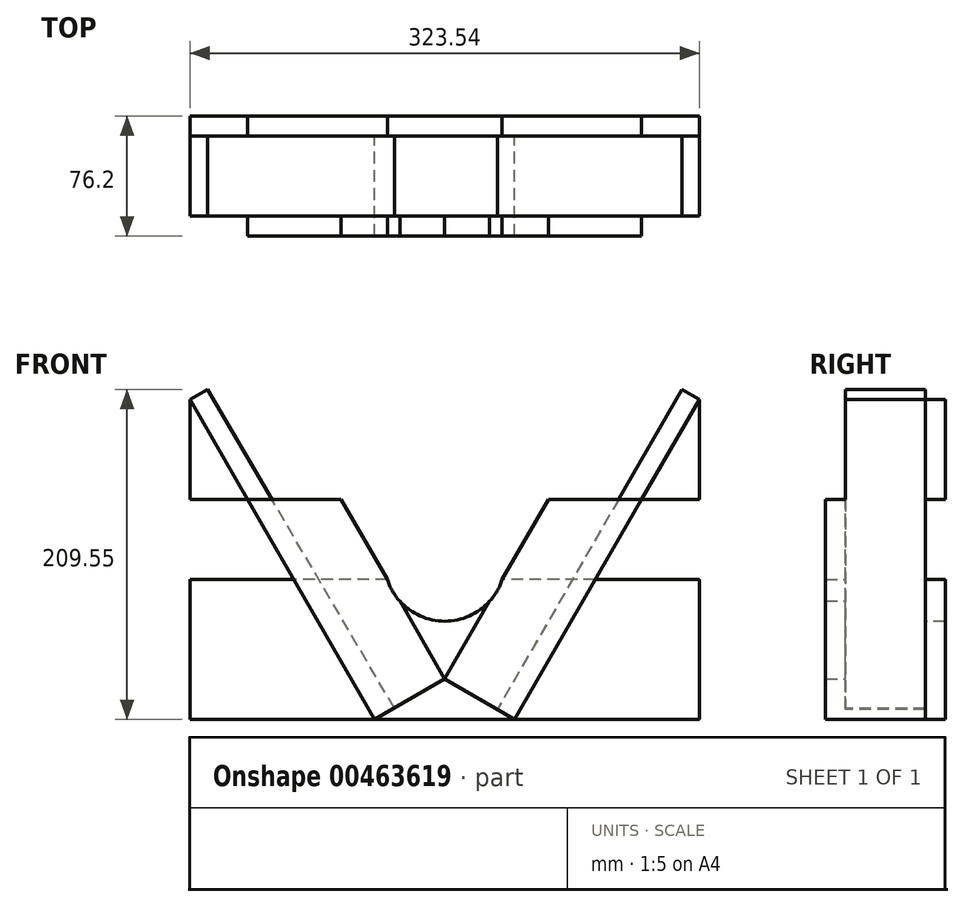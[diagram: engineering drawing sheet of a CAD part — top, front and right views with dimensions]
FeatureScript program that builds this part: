
annotation { "Feature Type Name" : "Feature", "Feature Type Description" : "" }
export const myFeature = defineFeature(function(context is Context, id is Id, definition is map)
    precondition{}
    {
        {
            var Q0;
            Q0=qCreatedBy(makeId("Front.planeOp"),FACE);
            var sketch = newSketch(context, id + "F0", { "sketchPlane" : qUnion([Q0])});
            skLineSegment(sketch, "E0.bottom", {"start": v(44.45, 101.6) * mm, "end": v(-44.45, 101.6) * mm});
            skLineSegment(sketch, "E0.top", {"start": v(44.45, -101.6) * mm, "end": v(-44.45, -101.6) * mm});
            skLineSegment(sketch, "E0.left", {"start": v(44.45, 101.6) * mm, "end": v(44.45, -101.6) * mm});
            skLineSegment(sketch, "E0.right", {"start": v(-44.45, 101.6) * mm, "end": v(-44.45, -101.6) * mm});
            skPoint(sketch, "E0.middle", {"position": v(0, 0) * mm});
            skLineSegment(sketch, "E1", {"start": v(-44.45, -101.6) * mm, "end": v(-161.77, 101.6) * mm});
            skLineSegment(sketch, "E2", {"start": v(44.45, -101.6) * mm, "end": v(161.77, 101.6) * mm});
            skLineSegment(sketch, "E3", {"start": v(-44.45, 101.6) * mm, "end": v(-161.77, 101.6) * mm});
            skLineSegment(sketch, "E4", {"start": v(44.45, 101.6) * mm, "end": v(161.77, 101.6) * mm});
            skLineSegment(sketch, "E5", {"start": v(44.45, -101.6) * mm, "end": v(0, -75.94) * mm});
            skLineSegment(sketch, "E6", {"start": v(0, -75.94) * mm, "end": v(117.42, 127.44) * mm});
            skLineSegment(sketch, "E7", {"start": v(117.42, 127.44) * mm, "end": v(161.77, 101.6) * mm});
            skLineSegment(sketch, "E8", {"start": v(-44.45, -101.6) * mm, "end": v(0, -75.94) * mm});
            skLineSegment(sketch, "E9", {"start": v(0, -75.94) * mm, "end": v(-117.34, 127.3) * mm});
            skLineSegment(sketch, "E10", {"start": v(-117.34, 127.3) * mm, "end": v(-161.77, 101.6) * mm});
            skLineSegment(sketch, "E11.bottom", {"start": v(161.77, 101.6) * mm, "end": v(-161.77, 101.6) * mm});
            skLineSegment(sketch, "E11.top", {"start": v(161.77, 38.1) * mm, "end": v(-161.77, 38.1) * mm});
            skLineSegment(sketch, "E11.left", {"start": v(161.77, 101.6) * mm, "end": v(161.77, 38.1) * mm});
            skLineSegment(sketch, "E11.right", {"start": v(-161.77, 101.6) * mm, "end": v(-161.77, 38.1) * mm});
            skLineSegment(sketch, "E12", {"start": v(102.5, 101.6) * mm, "end": v(161.77, 101.6) * mm});
            skLineSegment(sketch, "E13", {"start": v(-103.1, 101.6) * mm, "end": v(-161.77, 101.6) * mm});
            skLineSegment(sketch, "E14", {"start": v(-161.77, 101.6) * mm, "end": v(-103.1, 101.6) * mm});
            skLineSegment(sketch, "E15.bottom", {"start": v(161.77, -101.6) * mm, "end": v(-161.77, -101.6) * mm});
            skLineSegment(sketch, "E15.top", {"start": v(161.77, -12.7) * mm, "end": v(-161.77, -12.7) * mm});
            skLineSegment(sketch, "E15.left", {"start": v(161.77, -101.6) * mm, "end": v(161.77, -12.7) * mm});
            skLineSegment(sketch, "E15.right", {"start": v(-161.77, -101.6) * mm, "end": v(-161.77, -12.7) * mm});
            skLineSegment(sketch, "E16", {"start": v(44.45, 101.6) * mm, "end": v(44.45, 38.1) * mm});
            skLineSegment(sketch, "E17", {"start": v(-44.45, 101.6) * mm, "end": v(-44.45, 38.1) * mm});
            skArc(sketch, "E18", {"start": v(-36.5, -12.7) * mm, "mid": v(0, -39.2) * mm, "end": v(36.5, -12.7) * mm});
            skPoint(sketch, "E18.startSnap0", {"position": v(0, -12.7) * mm});
            skPoint(sketch, "E18.endSnap0", {"position": v(0, -12.7) * mm});
            skSolve(sketch);
        }
        {
            var Q0;
            {var subQ0=sQuery(id+"F0.wireOp",EDGE,"E2");Q0=makeQuery(id+"F0.imprint","IMPRINT",FACE,{"disambiguationData":[TD([[makeQuery(id+"F0.imprint","IMPRINT",EDGE,{"derivedFrom":subQ0}),1.0]])]});}
            var Q1;
            {var subQ0=sQuery(id+"F0.wireOp",EDGE,"E5");Q1=makeQuery(id+"F0.imprint","IMPRINT",FACE,{"disambiguationData":[TD([[makeQuery(id+"F0.imprint","IMPRINT",EDGE,{"derivedFrom":subQ0}),-1.0]])]});}
            var Q2;
            {var subQ0=sQuery(id+"F0.wireOp",EDGE,"E1");Q2=makeQuery(id+"F0.imprint","IMPRINT",FACE,{"disambiguationData":[TD([[makeQuery(id+"F0.imprint","IMPRINT",EDGE,{"derivedFrom":subQ0}),-1.0]])]});}
            var Q3;
            {var subQ0=sQuery(id+"F0.wireOp",EDGE,"E8");Q3=makeQuery(id+"F0.imprint","IMPRINT",FACE,{"disambiguationData":[TD([[makeQuery(id+"F0.imprint","IMPRINT",EDGE,{"derivedFrom":subQ0}),1.0]])]});}
            var Q4;
            {var subQ5=sQuery(id+"F0.wireOp",EDGE,"E14");Q4=makeQuery(id+"F0.imprint","IMPRINT",FACE,{"disambiguationData":[TD([[makeQuery(id+"F0.imprint","IMPRINT",EDGE,{"derivedFrom":subQ5}),-1.0]])]});}
            var Q5;
            {var subQ3=sQuery(id+"F0.wireOp",EDGE,"E9");var subQ5=sQuery(id+"F0.wireOp",EDGE,"E0.right");var subQ6=makeQuery(id+"F0.imprint","INTERSECT",VERTEX,{"derivedFrom":[subQ5,subQ3]});Q5=makeQuery(id+"F0.imprint","IMPRINT",FACE,{"disambiguationData":[TD([[makeQuery(id+"F0.imprint","IMPRINT",EDGE,{"disambiguationData":[TD([[subQ6,-1.0]])],"derivedFrom":subQ5}),-1.0]])]});}
            var Q6;
            {var subQ3=sQuery(id+"F0.wireOp",EDGE,"E6");var subQ5=sQuery(id+"F0.wireOp",EDGE,"E0.left");var subQ6=makeQuery(id+"F0.imprint","INTERSECT",VERTEX,{"derivedFrom":[subQ5,subQ3]});Q6=makeQuery(id+"F0.imprint","IMPRINT",FACE,{"disambiguationData":[TD([[makeQuery(id+"F0.imprint","IMPRINT",EDGE,{"disambiguationData":[TD([[subQ6,-1.0]])],"derivedFrom":subQ5}),1.0]])]});}
            var Q7;
            {var subQ0=sQuery(id+"F0.wireOp",EDGE,"E6");var subQ1=sQuery(id+"F0.wireOp",EDGE,"E0.left");var subQ2=makeQuery(id+"F0.imprint","INTERSECT",VERTEX,{"derivedFrom":[subQ1,subQ0]});Q7=makeQuery(id+"F0.imprint","IMPRINT",FACE,{"disambiguationData":[TD([[makeQuery(id+"F0.imprint","IMPRINT",EDGE,{"disambiguationData":[TD([[subQ2,-1.0]])],"derivedFrom":subQ1}),-1.0]])]});}
            var Q8;
            {var subQ0=sQuery(id+"F0.wireOp",EDGE,"E9");var subQ1=sQuery(id+"F0.wireOp",EDGE,"E0.right");var subQ2=makeQuery(id+"F0.imprint","INTERSECT",VERTEX,{"derivedFrom":[subQ1,subQ0]});Q8=makeQuery(id+"F0.imprint","IMPRINT",FACE,{"disambiguationData":[TD([[makeQuery(id+"F0.imprint","IMPRINT",EDGE,{"disambiguationData":[TD([[subQ2,-1.0]])],"derivedFrom":subQ1}),1.0]])]});}
            var Q9;
            {var subQ0=sQuery(id+"F0.wireOp",EDGE,"E12");Q9=makeQuery(id+"F0.imprint","IMPRINT",FACE,{"disambiguationData":[TD([[makeQuery(id+"F0.imprint","IMPRINT",EDGE,{"derivedFrom":subQ0}),-1.0]])]});}
            extrude(context, id + "F1", {"entities" : qUnion([Q0, Q1, Q2, Q3, Q4, Q5, Q6, Q7, Q8, Q9]), "depth" : 12.7 * mm, "offsetDistance" : 25.4 * mm});
        }
        {
            var Q0;
            Q0=makeQuery(id+"F1.opExtrude","CAP_FACE",FACE,{"disambiguationData":[OSD([sQuery(id+"F0.wireOp",EDGE,"E1"),sQuery(id+"F0.wireOp",EDGE,"E8"),sQuery(id+"F0.wireOp",EDGE,"E9"),sQuery(id+"F0.wireOp",EDGE,"E11.bottom"),sQuery(id+"F0.wireOp",EDGE,"E14")])],"isStart":true});
            var sketch = newSketch(context, id + "F2", { "sketchPlane" : qUnion([Q0])});
            skLineSegment(sketch, "E19", {"start": v(161.77, 101.6) * mm, "end": v(44.45, -101.6) * mm});
            skLineSegment(sketch, "E20", {"start": v(44.45, -101.6) * mm, "end": v(32.05, -94.44) * mm});
            skLineSegment(sketch, "E21", {"start": v(32.05, -94.44) * mm, "end": v(150.77, 107.95) * mm});
            skLineSegment(sketch, "E22", {"start": v(150.77, 107.95) * mm, "end": v(161.77, 101.6) * mm});
            skSolve(sketch);
        }
        {
            var Q0;
            Q0 = qSketchRegion(id + "F2", true);
            extrude(context, id + "F3", {"entities" : qUnion([Q0]), "operationType" : NewBodyOperationType.ADD, "depth" : 50.8 * mm, "offsetDistance" : 25.4 * mm});
        }
        {
            var Q0;
            Q0=makeQuery(id+"F1.opExtrude","CAP_FACE",FACE,{"disambiguationData":[OSD([sQuery(id+"F0.wireOp",EDGE,"E2"),sQuery(id+"F0.wireOp",EDGE,"E5"),sQuery(id+"F0.wireOp",EDGE,"E6"),sQuery(id+"F0.wireOp",EDGE,"E12")])],"isStart":true});
            var sketch = newSketch(context, id + "F4", { "sketchPlane" : qUnion([Q0])});
            skLineSegment(sketch, "E23", {"start": v(-161.77, 101.6) * mm, "end": v(-150.77, 107.95) * mm});
            skLineSegment(sketch, "E24", {"start": v(-150.77, 107.95) * mm, "end": v(-33.45, -95.25) * mm});
            skLineSegment(sketch, "E25", {"start": v(-33.45, -95.25) * mm, "end": v(-44.45, -101.6) * mm});
            skLineSegment(sketch, "E26", {"start": v(-44.45, -101.6) * mm, "end": v(-161.77, 101.6) * mm});
            skSolve(sketch);
        }
        {
            var Q0;
            Q0 = qSketchRegion(id + "F4", true);
            extrude(context, id + "F5", {"entities" : qUnion([Q0]), "operationType" : NewBodyOperationType.ADD, "depth" : 50.8 * mm, "offsetDistance" : 25.4 * mm});
        }
        {
            var Q0;
            {var subQ0=sQuery(id+"F0.wireOp",EDGE,"E11.left");Q0=makeQuery(id+"F0.imprint","IMPRINT",FACE,{"disambiguationData":[TD([[makeQuery(id+"F0.imprint","IMPRINT",EDGE,{"derivedFrom":subQ0}),-1.0]])]});}
            var Q1;
            {var subQ1=sQuery(id+"F0.wireOp",EDGE,"E6");var subQ3=sQuery(id+"F0.wireOp",EDGE,"E18");var subQ4=makeQuery(id+"F0.imprint","INTERSECT",VERTEX,{"derivedFrom":[subQ1,subQ3]});Q1=makeQuery(id+"F0.imprint","IMPRINT",FACE,{"disambiguationData":[TD([[makeQuery(id+"F0.imprint","IMPRINT",EDGE,{"disambiguationData":[TD([[subQ4,1.0]])],"derivedFrom":subQ3}),-1.0]])]});}
            var Q2;
            {var subQ5=sQuery(id+"F0.wireOp",EDGE,"E16");Q2=makeQuery(id+"F0.imprint","IMPRINT",FACE,{"disambiguationData":[TD([[makeQuery(id+"F0.imprint","IMPRINT",EDGE,{"derivedFrom":subQ5}),1.0]])]});}
            var Q3;
            {var subQ0=sQuery(id+"F0.wireOp",EDGE,"E5");Q3=makeQuery(id+"F0.imprint","IMPRINT",FACE,{"disambiguationData":[TD([[makeQuery(id+"F0.imprint","IMPRINT",EDGE,{"derivedFrom":subQ0}),1.0]])]});}
            var Q4;
            {var subQ5=sQuery(id+"F0.wireOp",EDGE,"E14");Q4=makeQuery(id+"F0.imprint","IMPRINT",FACE,{"disambiguationData":[TD([[makeQuery(id+"F0.imprint","IMPRINT",EDGE,{"derivedFrom":subQ5}),-1.0]])]});}
            var Q5;
            {var subQ5=sQuery(id+"F0.wireOp",EDGE,"E17");Q5=makeQuery(id+"F0.imprint","IMPRINT",FACE,{"disambiguationData":[TD([[makeQuery(id+"F0.imprint","IMPRINT",EDGE,{"derivedFrom":subQ5}),-1.0]])]});}
            var Q6;
            {var subQ5=sQuery(id+"F0.wireOp",EDGE,"E15.left");Q6=makeQuery(id+"F0.imprint","IMPRINT",FACE,{"disambiguationData":[TD([[makeQuery(id+"F0.imprint","IMPRINT",EDGE,{"derivedFrom":subQ5}),1.0]])]});}
            var Q7;
            {var subQ0=sQuery(id+"F0.wireOp",EDGE,"E2");var subQ3=sQuery(id+"F0.wireOp",EDGE,"E15.top");var subQ5=makeQuery(id+"F0.imprint","INTERSECT",VERTEX,{"derivedFrom":[subQ0,subQ3]});Q7=makeQuery(id+"F0.imprint","IMPRINT",FACE,{"disambiguationData":[TD([[makeQuery(id+"F0.imprint","IMPRINT",EDGE,{"disambiguationData":[TD([[subQ5,-1.0]])],"derivedFrom":subQ3}),1.0]])]});}
            var Q8;
            {var subQ5=sQuery(id+"F0.wireOp",EDGE,"E15.right");Q8=makeQuery(id+"F0.imprint","IMPRINT",FACE,{"disambiguationData":[TD([[makeQuery(id+"F0.imprint","IMPRINT",EDGE,{"derivedFrom":subQ5}),-1.0]])]});}
            var Q9;
            {var subQ1=sQuery(id+"F0.wireOp",EDGE,"E8");Q9=makeQuery(id+"F0.imprint","IMPRINT",FACE,{"disambiguationData":[TD([[makeQuery(id+"F0.imprint","IMPRINT",EDGE,{"derivedFrom":subQ1}),1.0]])]});}
            var Q10;
            {var subQ0=sQuery(id+"F0.wireOp",EDGE,"E1");var subQ3=sQuery(id+"F0.wireOp",EDGE,"E15.top");var subQ5=makeQuery(id+"F0.imprint","INTERSECT",VERTEX,{"derivedFrom":[subQ0,subQ3]});Q10=makeQuery(id+"F0.imprint","IMPRINT",FACE,{"disambiguationData":[TD([[makeQuery(id+"F0.imprint","IMPRINT",EDGE,{"disambiguationData":[TD([[subQ5,1.0]])],"derivedFrom":subQ3}),1.0]])]});}
            var Q11;
            {var subQ7=sQuery(id+"F0.wireOp",EDGE,"E5");Q11=makeQuery(id+"F0.imprint","IMPRINT",FACE,{"disambiguationData":[TD([[makeQuery(id+"F0.imprint","IMPRINT",EDGE,{"derivedFrom":subQ7}),-1.0]])]});}
            var Q12;
            {var subQ0=sQuery(id+"F0.wireOp",EDGE,"E12");Q12=makeQuery(id+"F0.imprint","IMPRINT",FACE,{"disambiguationData":[TD([[makeQuery(id+"F0.imprint","IMPRINT",EDGE,{"derivedFrom":subQ0}),-1.0]])]});}
            var Q13;
            {var subQ0=sQuery(id+"F0.wireOp",EDGE,"E11.right");Q13=makeQuery(id+"F0.imprint","IMPRINT",FACE,{"disambiguationData":[TD([[makeQuery(id+"F0.imprint","IMPRINT",EDGE,{"derivedFrom":subQ0}),1.0]])]});}
            extrude(context, id + "F8", {"entities" : qUnion([Q0, Q1, Q2, Q3, Q4, Q5, Q6, Q7, Q8, Q9, Q10, Q11, Q12, Q13]), "oppositeDirection" : true, "depth" : 63.5 * mm, "offsetDistance" : 25.4 * mm, "hasSecondDirection" : true, "secondDirectionOppositeDirection" : true, "secondDirectionDepth" : 50.8 * mm});
        }
    });
